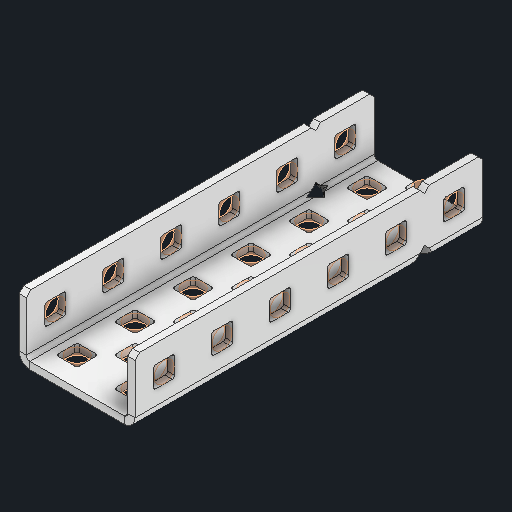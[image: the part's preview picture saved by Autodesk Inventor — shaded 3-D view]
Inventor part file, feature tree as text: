
AUTODESK INVENTOR PART (.ipt)
format: ipt  version: 2024 (Build 280153000, 153)  size: 700,928 bytes
history: native  units: in
note: dims shown in document units (in); Inventor stores cm internally (conversion verified against a paired STEP export)
features: other x37, extrude x28, sheet_metal_op x11, pattern_linear x2, mirror x1, chamfer x1, sketch x1
ambient origin geometry x8: Origin, YZ Plane, XZ Plane, XY Plane, X Axis, Y Axis, Z Axis, Center Point
bodies: Solid1 (feature_tree), Body (feature_tree)
feature tree (81):
  sheet_metal_op  "Flanges"
  other  "Flange Pattern Plane"
  other  "Flange Pattern Sketch"
  sheet_metal_op  "Flange Pattern"
  sheet_metal_op  "Body Pattern"
  pattern_linear  "Center Pattern"  Spacing1=3.0in  [1 undecoded]
  other  "Arc Length"
  mirror  "Notch Mirror"
  pattern_linear  "Notch Pattern"  Spacing1=0.0625in  [1 undecoded]
  chamfer  "End Chamfer"
  extrude  "Half Cut"  Depth=0.0625in
  other  "Plate1"
  sketch  "Sketch2"  dims[d0=1.0in d1=3.0in d2=0.0625in d3=0.0625in d4=0.0312in d5=0.125in d6=0.0625in d7=0.5in d8=90.0deg d9=0.0312in d10=0.25in d11=0.0625in d12=0.0625in d16=0.182in d17=0.02in d18=0.0625in d19=0.0in d20=0.25in d21=0.25in d38=2.3622in d40=0.5in d41=0.7874in d43=1.0in d46=0.172in d47=1.0in d48=0.0in d49=0.182in d50=0.02in d51=0.25in d52=0.25in d53=0.0625in d54=0.0in d55=0.172in d56=1.0in d57=0.0in d58=0.25in d60=2.3622in d62=0.5in d63=0.7874in d65=0.5in d85=0.1473in d86=0.1782in d88=0.04in d89=0.0625in d90=0.0in d91=0.04in d92=0.0491in d95=2.5in d96=0.04in d97=0.25in d98=45.0deg d99=0.25in d100=0.5in d101=0.0in d102=2.497in d106=0.182in d107=0.02in d108=0.5in d109=0.5in d110=0.0625in d111=0.0in d112=0.172in d113=0.5in d114=0.0in d117=0.5in d118=0.5in d119=0.5in]
  other  "Plate2"
  sheet_metal_op  "Bend1"
  sheet_metal_op  "Corner1"
  other  "Srf1"
  other  "Srf2"
  other  "Srf91"
  sheet_metal_op  "Body Pattern Sketch"
  other  "Srf92"
  other  "Srf786"
  other  "Srf823"
  other  "Srf824"
  other  "Srf825"
  other  "Srf826"
  other  "Srf827"
  other  "Srf828"
  other  "Srf829"
  other  "Srf856"
  other  "Srf857"
  other  "Srf858"
  other  "Srf859"
  other  "Srf860"
  other  "Srf861"
  other  "Srf862"
  other  "Srf889"
  other  "Srf890"
  other  "Srf891"
  other  "Srf892"
  other  "Srf893"
  other  "Srf922"
  other  "Srf923"
  other  "Srf924"
  other  "Srf959"
  other  "Srf960"
  other  "Srf961"
  sheet_metal_op  "Flange Stamp"
  sheet_metal_op  "Flange Circle"
  sheet_metal_op  "Body Stamp"
  sheet_metal_op  "Body Circle"
  other  "Center Stamp"
  other  "Center Circle"
  sheet_metal_op  "Notch"
  extrude  "ExtrusionSrf2"  Depth=0.0312in
  extrude  "ExtrusionSrf92"  Depth=0.5in
  extrude  "ExtrusionSrf823"  Depth=0.0625in
  extrude  "ExtrusionSrf824"  Depth=0.5in TaperAngle=90.0deg
  extrude  "ExtrusionSrf825"  Depth=0.5in
  extrude  "ExtrusionSrf826"  Depth=0.0625in
  extrude  "ExtrusionSrf827"  Depth=0.0625in
  extrude  "ExtrusionSrf828"  Depth=0.5in
  extrude  "ExtrusionSrf829"  Depth=0.02in
  extrude  "ExtrusionSrf856"  Depth=0.0625in
  extrude  "ExtrusionSrf857"  TaperAngle=0.0deg  [1 undecoded]
  extrude  "ExtrusionSrf858"  Depth=0.5in
  extrude  "ExtrusionSrf859"  Depth=0.5in
  extrude  "ExtrusionSrf860"  Depth=0.5in
  extrude  "ExtrusionSrf861"  Depth=0.5in
  extrude  "ExtrusionSrf862"  Depth=1.0in TaperAngle=0.0deg
  extrude  "ExtrusionSrf889"  Depth=0.5in
  extrude  "ExtrusionSrf890"  Depth=0.02in
  extrude  "ExtrusionSrf891"  Depth=0.5in
  extrude  "ExtrusionSrf892"  Depth=0.5in
  extrude  "ExtrusionSrf893"  Depth=0.0625in
  extrude  "ExtrusionSrf922"  TaperAngle=0.0deg  [1 undecoded]
  extrude  "ExtrusionSrf923"  Depth=0.5in
  extrude  "ExtrusionSrf924"  Depth=1.0in TaperAngle=0.0deg
  extrude  "ExtrusionSrf959"  Depth=0.5in
  extrude  "ExtrusionSrf960"  Depth=0.5in
  extrude  "ExtrusionSrf961"  Depth=0.5in
note: 4 required parameter values undecoded (feature->parameter linkage not recoverable at this tier; creation-order binding heuristic only, values carry confidence <= 0.55)
